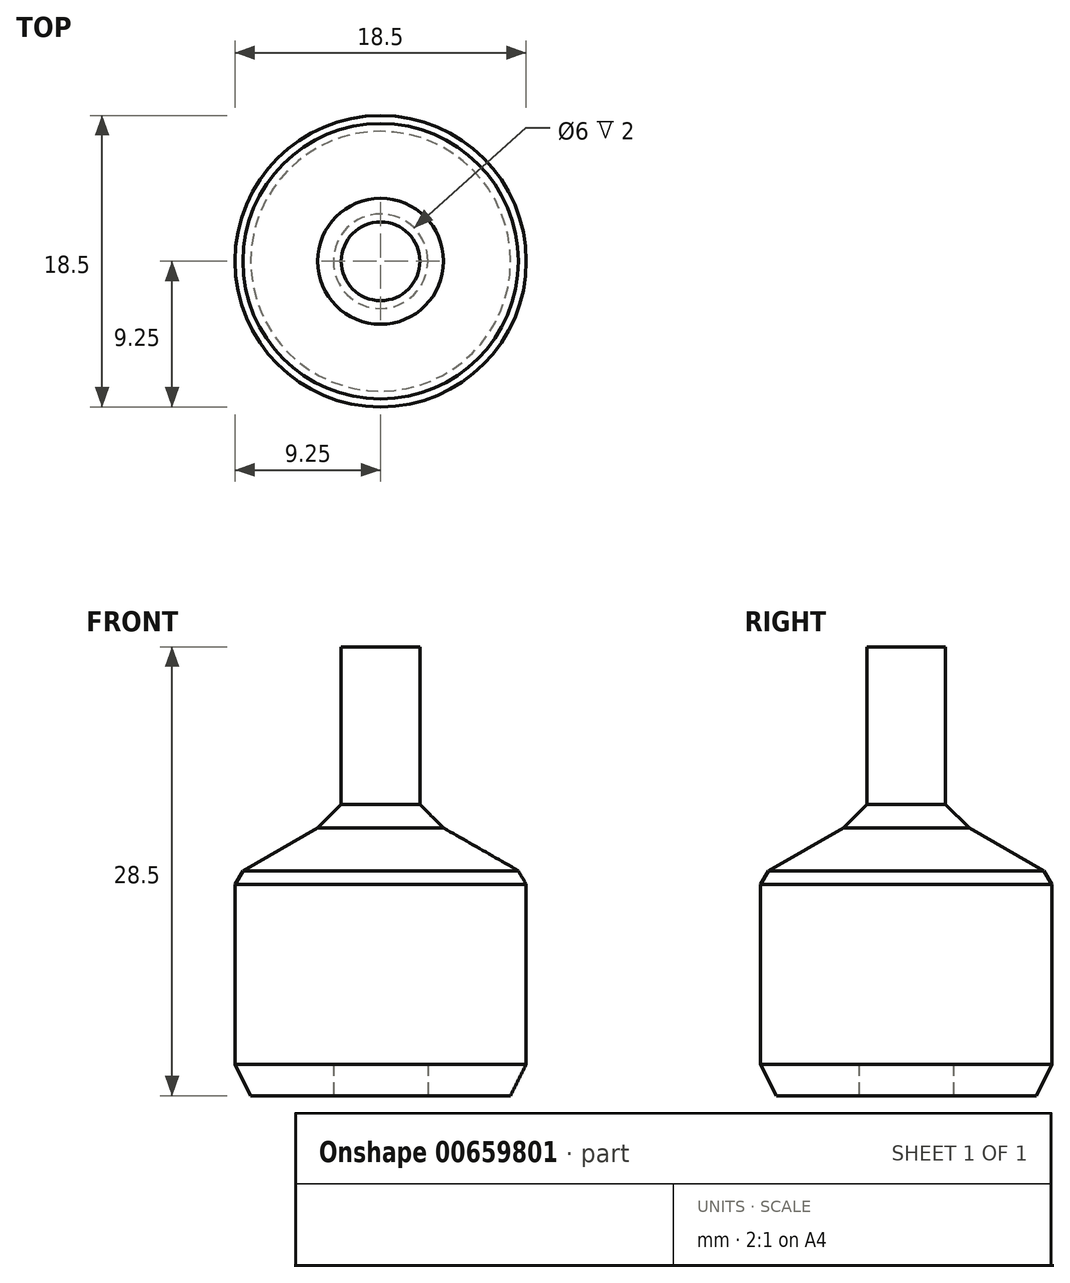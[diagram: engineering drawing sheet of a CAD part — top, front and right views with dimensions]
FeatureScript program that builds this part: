
annotation { "Feature Type Name" : "Feature", "Feature Type Description" : "" }
export const myFeature = defineFeature(function(context is Context, id is Id, definition is map)
    precondition{}
    {
        {
            var Q0;
            Q0=qCreatedBy(makeId("Top.planeOp"),FACE);
            cPlane(context, id + "F0", {"entities" : qUnion([Q0]), "cplaneType" : CPlaneType.OFFSET, "offset" : 2 * mm, "width" : 152.4 * mm, "height" : 152.4 * mm});
        }
        {
            var Q0;
            Q0=qCreatedBy(id+"F0.planeOp",FACE);
            cPlane(context, id + "F1", {"entities" : qUnion([Q0]), "cplaneType" : CPlaneType.OFFSET, "offset" : 12 * mm, "width" : 150 * mm, "height" : 150 * mm});
        }
        {
            var Q0;
            Q0=qCreatedBy(id+"F1.planeOp",FACE);
            cPlane(context, id + "F2", {"entities" : qUnion([Q0]), "cplaneType" : CPlaneType.OFFSET, "offset" : 3 * mm, "width" : 150 * mm, "height" : 150 * mm});
        }
        {
            var Q0;
            Q0=qCreatedBy(makeId("Top.planeOp"),FACE);
            cPlane(context, id + "F3", {"entities" : qUnion([Q0]), "cplaneType" : CPlaneType.OFFSET, "offset" : 18.5 * mm, "width" : 150 * mm, "height" : 150 * mm});
        }
        {
            var Q0;
            Q0=qCreatedBy(id+"F3.planeOp",FACE);
            cPlane(context, id + "F4", {"entities" : qUnion([Q0]), "cplaneType" : CPlaneType.OFFSET, "offset" : 10 * mm, "width" : 150 * mm, "height" : 150 * mm});
        }
        {
            var Q0;
            Q0=qCreatedBy(makeId("Top.planeOp"),FACE);
            var sketch = newSketch(context, id + "F5", { "sketchPlane" : qUnion([Q0])});
            skCircle(sketch, "E0", {"center": v(0, 0) * mm, "radius": 8.25 * mm});
            skSolve(sketch);
        }
        {
            var Q0;
            Q0=qCreatedBy(id+"F0.planeOp",FACE);
            var sketch = newSketch(context, id + "F6", { "sketchPlane" : qUnion([Q0])});
            skCircle(sketch, "E1", {"center": v(0, 0) * mm, "radius": 9.25 * mm});
            skSolve(sketch);
        }
        {
            var Q0;
            Q0=qCreatedBy(id+"F1.planeOp",FACE);
            var sketch = newSketch(context, id + "F7", { "sketchPlane" : qUnion([Q0])});
            skCircle(sketch, "E2", {"center": v(0, 0) * mm, "radius": 9.25 * mm});
            skSolve(sketch);
        }
        {
            var Q0;
            Q0=qCreatedBy(id+"F3.planeOp",FACE);
            var sketch = newSketch(context, id + "F8", { "sketchPlane" : qUnion([Q0])});
            skCircle(sketch, "E3", {"center": v(0, 0) * mm, "radius": 2.5 * mm});
            skSolve(sketch);
        }
        {
            var Q0;
            Q0=qCreatedBy(id+"F2.planeOp",FACE);
            var sketch = newSketch(context, id + "F9", { "sketchPlane" : qUnion([Q0])});
            skCircle(sketch, "E4", {"center": v(0, 0) * mm, "radius": 4 * mm});
            skSolve(sketch);
        }
        {
            var Q0;
            Q0=qCreatedBy(id+"F4.planeOp",FACE);
            var sketch = newSketch(context, id + "F10", { "sketchPlane" : qUnion([Q0])});
            skCircle(sketch, "E5", {"center": v(0, 0) * mm, "radius": 2.5 * mm});
            skSolve(sketch);
        }
        {
            var Q0;
            Q0=makeQuery(id+"F5.imprint","IMPRINT",FACE,{"disambiguationData":[TD([[makeQuery(id+"F5.imprint","IMPRINT",EDGE,{"derivedFrom":sQuery(id+"F5.wireOp",EDGE,"E0")}),1.0]])]});
            var Q1;
            Q1=makeQuery(id+"F6.imprint","IMPRINT",FACE,{"disambiguationData":[TD([[makeQuery(id+"F6.imprint","IMPRINT",EDGE,{"derivedFrom":sQuery(id+"F6.wireOp",EDGE,"E1")}),1.0]])]});
            loft(context, id + "F11", {"sheetProfilesArray" : [{ "sheetProfileEntities" : qUnion([Q0]) }, { "sheetProfileEntities" : qUnion([Q1]) }]});
        }
        {
            var Q1;
            Q1=makeQuery(id+"F11.opLoft","CAP_FACE",FACE,{"disambiguationData":[OSD([makeQuery(id+"F6.imprint","IMPRINT",FACE,{"disambiguationData":[TD([[makeQuery(id+"F6.imprint","IMPRINT",EDGE,{"derivedFrom":sQuery(id+"F6.wireOp",EDGE,"E1")}),1.0]])]})])],"isStart":true});
            var Q2;
            Q2=makeQuery(id+"F7.imprint","IMPRINT",FACE,{"disambiguationData":[TD([[makeQuery(id+"F7.imprint","IMPRINT",EDGE,{"derivedFrom":sQuery(id+"F7.wireOp",EDGE,"E2")}),1.0]])]});
            loft(context, id + "F12", {"operationType" : NewBodyOperationType.ADD, "sheetProfilesArray" : [{ "sheetProfileEntities" : qUnion([Q1]) }, { "sheetProfileEntities" : qUnion([Q2]) }]});
        }
        {
            var Q1;
            Q1=makeQuery(id+"F12.opLoft","CAP_FACE",FACE,{"disambiguationData":[OSD([makeQuery(id+"F7.imprint","IMPRINT",FACE,{"disambiguationData":[TD([[makeQuery(id+"F7.imprint","IMPRINT",EDGE,{"derivedFrom":sQuery(id+"F7.wireOp",EDGE,"E2")}),1.0]])]})])],"isStart":true});
            var Q2;
            Q2=makeQuery(id+"F9.imprint","IMPRINT",FACE,{"disambiguationData":[TD([[makeQuery(id+"F9.imprint","IMPRINT",EDGE,{"derivedFrom":sQuery(id+"F9.wireOp",EDGE,"E4")}),1.0]])]});
            loft(context, id + "F13", {"operationType" : NewBodyOperationType.ADD, "sheetProfilesArray" : [{ "sheetProfileEntities" : qUnion([Q1]) }, { "sheetProfileEntities" : qUnion([Q2]) }]});
        }
        {
            var Q1;
            Q1=makeQuery(id+"F13.opLoft","CAP_FACE",FACE,{"disambiguationData":[OSD([makeQuery(id+"F9.imprint","IMPRINT",FACE,{"disambiguationData":[TD([[makeQuery(id+"F9.imprint","IMPRINT",EDGE,{"derivedFrom":sQuery(id+"F9.wireOp",EDGE,"E4")}),1.0]])]})])],"isStart":true});
            var Q2;
            Q2=makeQuery(id+"F8.imprint","IMPRINT",FACE,{"disambiguationData":[TD([[makeQuery(id+"F8.imprint","IMPRINT",EDGE,{"derivedFrom":sQuery(id+"F8.wireOp",EDGE,"E3")}),1.0]])]});
            loft(context, id + "F14", {"operationType" : NewBodyOperationType.ADD, "sheetProfilesArray" : [{ "sheetProfileEntities" : qUnion([Q1]) }, { "sheetProfileEntities" : qUnion([Q2]) }]});
        }
        {
            var Q1;
            Q1=makeQuery(id+"F14.opLoft","CAP_FACE",FACE,{"disambiguationData":[OSD([makeQuery(id+"F8.imprint","IMPRINT",FACE,{"disambiguationData":[TD([[makeQuery(id+"F8.imprint","IMPRINT",EDGE,{"derivedFrom":sQuery(id+"F8.wireOp",EDGE,"E3")}),1.0]])]})])],"isStart":true});
            var Q2;
            Q2=makeQuery(id+"F10.imprint","IMPRINT",FACE,{"disambiguationData":[TD([[makeQuery(id+"F10.imprint","IMPRINT",EDGE,{"derivedFrom":sQuery(id+"F10.wireOp",EDGE,"E5")}),1.0]])]});
            loft(context, id + "F15", {"operationType" : NewBodyOperationType.ADD, "sheetProfilesArray" : [{ "sheetProfileEntities" : qUnion([Q1]) }, { "sheetProfileEntities" : qUnion([Q2]) }]});
        }
        {
            var Q0;
            {var subQ0=sQuery(id+"F7.wireOp",EDGE,"E2");var subQ1=sQuery(id+"F6.wireOp",EDGE,"E1");var subQ2=sQuery(id+"F5.wireOp",EDGE,"E0");Q0=makeQuery(id+"F13.boolean.opBoolean","MERGE",EDGE,{"derivedFrom":[makeQuery(id+"F12.opLoft","MID_CAP_EDGE",EDGE,{"disambiguationData":[OSD([subQ2,subQ1,subQ0])],"capPos":1.0}),makeQuery(id+"F13.opLoft","MID_CAP_EDGE",EDGE,{"disambiguationData":[OSD([subQ2,subQ1,subQ0])],"capPos":0.0})]});}
            chamfer(context, id + "F16", {"entities" : qUnion([Q0]), "width" : 1 * mm, "tangentPropagation" : true});
        }
        {
            var Q0;
            Q0=qCreatedBy(makeId("Top.planeOp"),FACE);
            var sketch = newSketch(context, id + "F17", { "sketchPlane" : qUnion([Q0])});
            skCircle(sketch, "E6", {"center": v(0, 0) * mm, "radius": 3 * mm});
            skSolve(sketch);
        }
        {
            var Q0;
            Q0=makeQuery(id+"F17.imprint","IMPRINT",FACE,{"disambiguationData":[TD([[makeQuery(id+"F17.imprint","IMPRINT",EDGE,{"derivedFrom":sQuery(id+"F17.wireOp",EDGE,"E6")}),1.0]])]});
            extrude(context, id + "F18", {"entities" : qUnion([Q0]), "operationType" : NewBodyOperationType.REMOVE, "depth" : 2 * mm});
        }
    });
